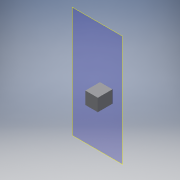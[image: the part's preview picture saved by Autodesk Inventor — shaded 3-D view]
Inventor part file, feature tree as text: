
AUTODESK INVENTOR PART (.ipt)
format: ipt  version: 2016 (Build 200138000, 138)  size: 91,648 bytes
history: native  units: in
note: dims shown in document units (in); Inventor stores cm internally (conversion verified against a paired STEP export)
features: plane x1, extrude x1, sketch x1, reference x1
ambient origin geometry x8: Origin, YZ Plane, XZ Plane, XY Plane, X Axis, Y Axis, Z Axis, Center Point
bodies: Solid1 (feature_tree)
feature tree (4):
  plane  "Work Plane1"
  extrude  "Extrusion1"  Depth=1.7in
  sketch  "Sketch1"  dims[d0=1.7in d1=1.7in d2=2.0in d3=0.0in]
  reference  "Reference1"
